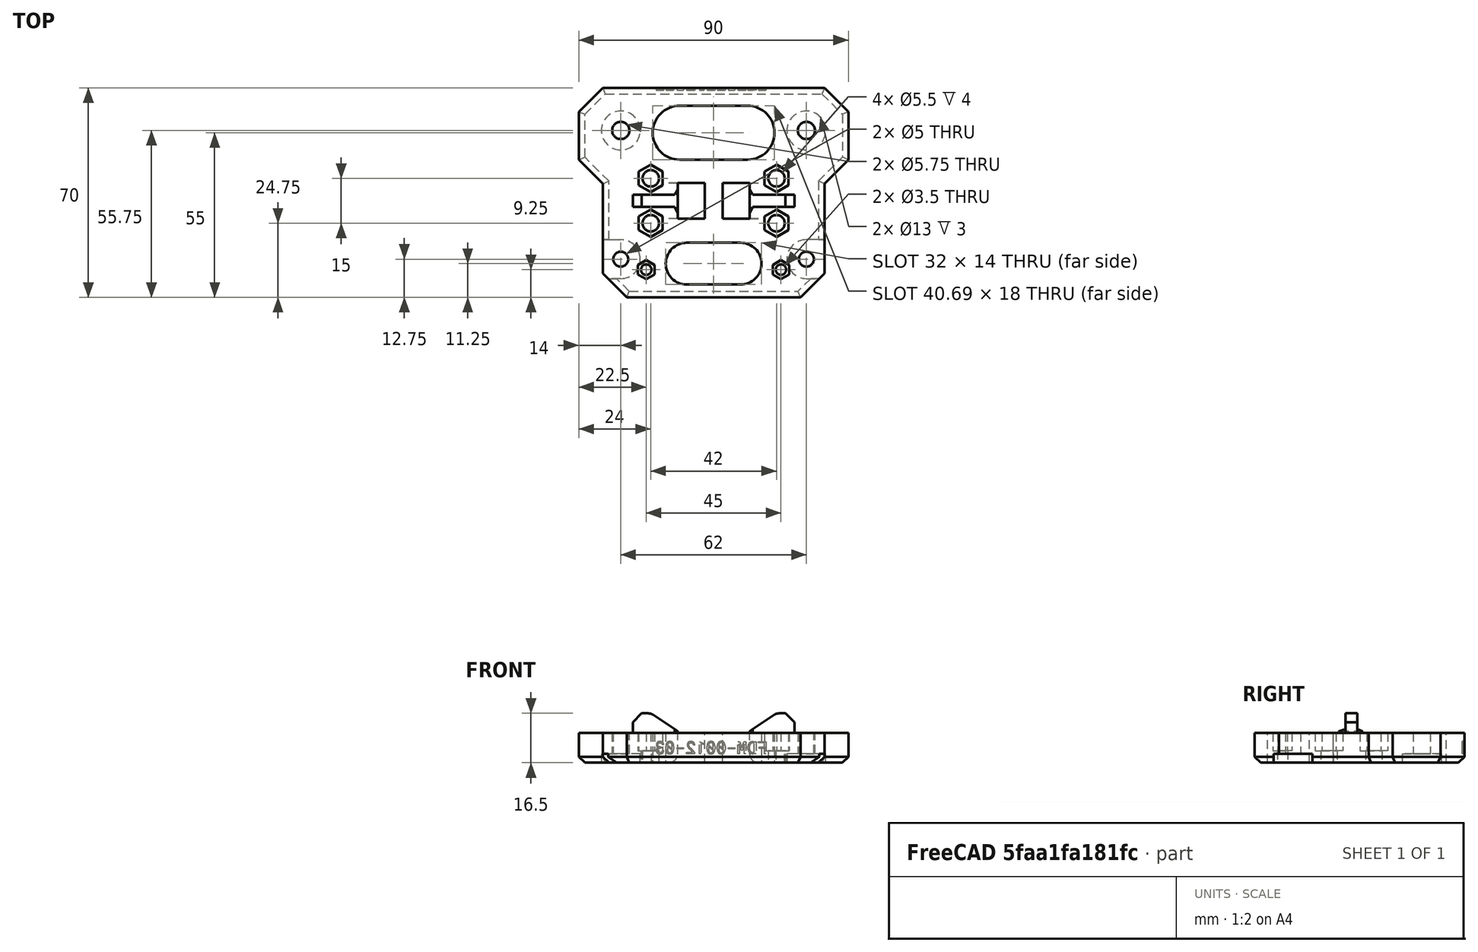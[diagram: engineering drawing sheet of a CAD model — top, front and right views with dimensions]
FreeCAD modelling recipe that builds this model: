
FCSTD DOCUMENT  (FreeCAD 0.20R29177 (Git))
Label: x-gantry-back
License: All rights reserved
LicenseURL: http://en.wikipedia.org/wiki/All_rights_reserved
objects: Sketcher::SketchObject×5, PartDesign::Plane×4, PartDesign::Chamfer×3, PartDesign::Pocket×3, PartDesign::Pad×2, Part::Part2DObjectPython×1, PartDesign::Fillet×1, PartDesign::Body×1, Mesh::Feature×1, Part::Extrusion×1, Part::Cut×1
note: 31 computed .brp shape members not serialized (recipe doc carries the construction recipe); baked Part::Feature solids carry a one-line shape summary decoded from their .brp

FEATURE [Sketcher::SketchObject] Sketch  label="Base"
  FullyConstrained = false
  MapMode = 5
  Support = -> [XY_Plane]
  sketch-geometry (58):
    g0: LineSegment StartX=0 StartY=0 StartZ=0 EndX=0 EndY=41.5 EndZ=0
    g1: LineSegment StartX=-31 StartY=41.5 StartZ=0 EndX=31 EndY=41.5 EndZ=0
    g2: Circle CenterX=-31 CenterY=41.5 CenterZ=0 NormalX=0 NormalY=0 NormalZ=1 AngleXU=0 Radius=2.875
    g3: Circle CenterX=31 CenterY=41.5 CenterZ=0 NormalX=0 NormalY=0 NormalZ=1 AngleXU=0 Radius=2.875
    g4: ArcOfCircle CenterX=-31 CenterY=4.5 CenterZ=0 NormalX=0 NormalY=0 NormalZ=1 AngleXU=0 Radius=2.5 StartAngle=2e-16 EndAngle=3.14159
    g5: ArcOfCircle CenterX=-31 CenterY=-1.5 CenterZ=0 NormalX=0 NormalY=0 NormalZ=1 AngleXU=0 Radius=2.5 StartAngle=3.14159 EndAngle=6.28319
    g6: LineSegment StartX=-33.5 StartY=4.5 StartZ=0 EndX=-33.5 EndY=-1.5 EndZ=0
    g7: LineSegment StartX=-28.5 StartY=4.5 StartZ=0 EndX=-28.5 EndY=-1.5 EndZ=0
    g8: Circle CenterX=-31 CenterY=41.5 CenterZ=0 NormalX=0 NormalY=0 NormalZ=1 AngleXU=0 Radius=12.5
    g9: Circle CenterX=31 CenterY=41.5 CenterZ=0 NormalX=0 NormalY=0 NormalZ=1 AngleXU=0 Radius=12.5
    g10: LineSegment StartX=45 StartY=55.75 StartZ=0 EndX=45 EndY=31.75 EndZ=0
    g11: LineSegment StartX=-45 StartY=31.75 StartZ=0 EndX=-45 EndY=55.75 EndZ=0
    g12: LineSegment StartX=-21 StartY=25.5 StartZ=0 EndX=-21 EndY=10.5 EndZ=0
    g13: LineSegment StartX=-12 StartY=24 StartZ=0 EndX=-3 EndY=24 EndZ=0
    g14: LineSegment StartX=-3 StartY=24 StartZ=0 EndX=-3 EndY=12 EndZ=0
    g15: LineSegment StartX=-3 StartY=12 StartZ=0 EndX=-12 EndY=12 EndZ=0
    g16: LineSegment StartX=-12 StartY=12 StartZ=0 EndX=-12 EndY=24 EndZ=0
    g17: Circle CenterX=-21 CenterY=25.5 CenterZ=0 NormalX=0 NormalY=0 NormalZ=1 AngleXU=0 Radius=2.75
    g18: Circle CenterX=-21 CenterY=10.5 CenterZ=0 NormalX=0 NormalY=0 NormalZ=1 AngleXU=0 Radius=2.75
    g19: LineSegment StartX=-21 StartY=18 StartZ=0 EndX=21 EndY=18 EndZ=0
    g20: LineSegment StartX=21 StartY=25.5 StartZ=0 EndX=21 EndY=10.5 EndZ=0
    g21: Circle CenterX=21 CenterY=25.5 CenterZ=0 NormalX=0 NormalY=0 NormalZ=1 AngleXU=0 Radius=2.75
    g22: Circle CenterX=21 CenterY=10.5 CenterZ=0 NormalX=0 NormalY=0 NormalZ=1 AngleXU=0 Radius=2.75
    g23: LineSegment StartX=3 StartY=24 StartZ=0 EndX=12 EndY=24 EndZ=0
    g24: LineSegment StartX=12 StartY=24 StartZ=0 EndX=12 EndY=12 EndZ=0
    g25: LineSegment StartX=12 StartY=12 StartZ=0 EndX=3 EndY=12 EndZ=0
    g26: LineSegment StartX=3 StartY=12 StartZ=0 EndX=3 EndY=24 EndZ=0
    g27: LineSegment StartX=-22.5 StartY=-5 StartZ=0 EndX=22.5 EndY=-5 EndZ=0
    g28: Circle CenterX=-22.5 CenterY=-5 CenterZ=0 NormalX=0 NormalY=0 NormalZ=1 AngleXU=0 Radius=1.75
    g29: Circle CenterX=22.5 CenterY=-5 CenterZ=0 NormalX=0 NormalY=0 NormalZ=1 AngleXU=0 Radius=1.75
    g30: LineSegment StartX=45 StartY=55.75 StartZ=0 EndX=45 EndY=31.75 EndZ=0
    g31: ArcOfCircle CenterX=31 CenterY=4.5 CenterZ=0 NormalX=0 NormalY=0 NormalZ=1 AngleXU=0 Radius=2.5 StartAngle=2e-16 EndAngle=3.14159
    g32: ArcOfCircle CenterX=31 CenterY=-1.5 CenterZ=0 NormalX=0 NormalY=0 NormalZ=1 AngleXU=0 Radius=2.5 StartAngle=3.14159 EndAngle=6.28319
    g33: LineSegment StartX=28.5 StartY=4.5 StartZ=0 EndX=28.5 EndY=-1.5 EndZ=0
    g34: LineSegment StartX=33.5 StartY=4.5 StartZ=0 EndX=33.5 EndY=-1.5 EndZ=0
    g35: LineSegment StartX=37 StartY=23.75 StartZ=0 EndX=37 EndY=-6.25 EndZ=0
    g36: LineSegment StartX=37 StartY=-6.25 StartZ=0 EndX=29 EndY=-14.25 EndZ=0
    g37: LineSegment StartX=-29 StartY=-14.25 StartZ=0 EndX=-37 EndY=-6.25 EndZ=0
    g38: LineSegment StartX=-37 StartY=-6.25 StartZ=0 EndX=-37 EndY=23.75 EndZ=0
    g39: LineSegment StartX=-37 StartY=23.75 StartZ=0 EndX=-45 EndY=31.75 EndZ=0
    g40: LineSegment StartX=37 StartY=23.75 StartZ=0 EndX=45 EndY=31.75 EndZ=0
    g41: LineSegment StartX=-29 StartY=-14.25 StartZ=0 EndX=29 EndY=-14.25 EndZ=0
    g42: ArcOfCircle CenterX=-9 CenterY=-3 CenterZ=0 NormalX=0 NormalY=0 NormalZ=1 AngleXU=0 Radius=7 StartAngle=1.5708 EndAngle=4.71239
    g43: ArcOfCircle CenterX=9 CenterY=-3 CenterZ=0 NormalX=0 NormalY=0 NormalZ=1 AngleXU=0 Radius=7 StartAngle=4.71239 EndAngle=7.85398
    g44: LineSegment StartX=-9 StartY=-10 StartZ=0 EndX=9 EndY=-10 EndZ=0
    g45: LineSegment StartX=-9 StartY=4 StartZ=0 EndX=9 EndY=4 EndZ=0
    g46: ArcOfCircle CenterX=-11.3452 CenterY=40.75 CenterZ=0 NormalX=0 NormalY=0 NormalZ=1 AngleXU=0 Radius=9 StartAngle=1.5708 EndAngle=4.71239
    g47: ArcOfCircle CenterX=11.3452 CenterY=40.75 CenterZ=0 NormalX=0 NormalY=0 NormalZ=1 AngleXU=0 Radius=9 StartAngle=4.71239 EndAngle=7.85398
    g48: LineSegment StartX=-11.3452 StartY=31.75 StartZ=0 EndX=11.3452 EndY=31.75 EndZ=0
    g49: LineSegment StartX=-11.3452 StartY=49.75 StartZ=0 EndX=11.3452 EndY=49.75 EndZ=0
    g50: LineSegment StartX=45 StartY=55.75 StartZ=0 EndX=-45 EndY=55.75 EndZ=0
    g51: Circle CenterX=-31 CenterY=-1.5 CenterZ=0 NormalX=0 NormalY=0 NormalZ=1 AngleXU=0 Radius=2.5
    g52: Circle CenterX=31 CenterY=-1.5 CenterZ=0 NormalX=0 NormalY=0 NormalZ=1 AngleXU=0 Radius=2.5
    g53: LineSegment StartX=-45 StartY=31.75 StartZ=0 EndX=-45 EndY=47.75 EndZ=0
    g54: LineSegment StartX=-45 StartY=47.75 StartZ=0 EndX=-37 EndY=55.75 EndZ=0
    g55: LineSegment StartX=-37 StartY=55.75 StartZ=0 EndX=37 EndY=55.75 EndZ=0
    g56: LineSegment StartX=37 StartY=55.75 StartZ=0 EndX=45 EndY=47.75 EndZ=0
    g57: LineSegment StartX=45 StartY=47.75 StartZ=0 EndX=45 EndY=31.75 EndZ=0
  constraints (149):
    c: Coincident(g0,g-1)
    c: PointOnObject(g0,g1)
    c: Symmetric(g1,g1,g0)
    c: DistanceY(g0,g0) = 41.5
    c: DistanceX(g1,g1) = 62
    c: Coincident(g2,g1)
    c: Coincident(g3,g1)
    c: Tangent(g4,g7)
    c: Tangent(g4,g6)
    c: Tangent(g6,g5)
    c: Tangent(g7,g5)
    c: Vertical(g6)
    c: Coincident(g8,g2)
    c: Coincident(g9,g3)
    c: Diameter(g4) = 5
    c: DistanceY(g5,g4) = 6
    c: Diameter(g3) = 5.75
    c: Diameter(g2) = 5.75
    c: Diameter(g9) = 25
    c: Diameter(g8) = 25
    c: Vertical(g10)
    c: Vertical(g11)
    c: Symmetric(g11,g10,g-2)
    c: Equal(g10,g11)
    c: DistanceX(g11,g10) = 90
    c: DistanceY(g3,g10) = 14.25
    c: DistanceY(g12,g12) = 15
    c: Coincident(g13,g14)
    c: Coincident(g14,g15)
    c: Coincident(g15,g16)
    c: Coincident(g16,g13)
    c: Horizontal(g13)
    c: Horizontal(g15)
    c: Vertical(g14)
    c: DistanceX(g13,g13) = 9
    c: DistanceY(g16,g16) = 12
    c: Coincident(g17,g12)
    c: Coincident(g18,g12)
    c: Diameter(g17) = 5.5
    c: Diameter(g18) = 5.5
    c: PointOnObject(g19,g12)
    c: Symmetric(g19,g19,g-2)
    c: Symmetric(g17,g18,g19)
    c: Symmetric(g13,g15,g19)
    c: PointOnObject(g19,g20)
    c: Symmetric(g20,g20,g19)
    c: DistanceY(g20,g20) = 15
    c: Coincident(g22,g20)
    c: Diameter(g21) = 5.5
    c: Diameter(g22) = 5.5
    c: Distance(g13,g0) = 3
    c: Distance(g17,g0) = 21
    c: Coincident(g23,g24)
    c: Coincident(g24,g25)
    c: Coincident(g25,g26)
    c: Coincident(g26,g23)
    c: Horizontal(g23)
    c: Horizontal(g25)
    c: Vertical(g24)
    c: DistanceX(g23,g23) = 9
    c: DistanceY(g26,g26) = 12
    c: DistanceX(g-1,g23) = 3
    c: Symmetric(g23,g25,g19)
    c: Symmetric(g27,g27,g-2)
    c: DistanceY(g27,g-1) = 5
    c: DistanceX(g27,g27) = 45
    c: Coincident(g28,g27)
    c: Coincident(g29,g27)
    c: Diameter(g29) = 3.5
    c: DistanceY(g0,g4) = 4.5
    c: Vertical(g5,g4)
    c: Vertical(g4,g2)
    c: Tangent(g31,g34)
    c: Tangent(g31,g33)
    c: Tangent(g33,g32)
    c: Tangent(g34,g32)
    c: Vertical(g33)
    c: Equal(g4,g31) = 5
    c: Vertical(g32,g31)
    c: Horizontal(g31,g4)
    c: Vertical(g31,g3)
    c: Horizontal(g32,g5)
    c: Vertical(g35)
    c: Coincident(g36,g35)
    c: Coincident(g38,g37)
    c: Vertical(g38)
    c: Coincident(g39,g38)
    c: Coincident(g40,g35)
    c: Horizontal(g40,g39)
    c: Horizontal(g35,g38)
    c: DistanceX(g38,g35) = 74
    c: DistanceY(g36,g30) = 70
    c: Coincident(g41,g37)
    c: Coincident(g41,g36)
    c: Horizontal(g41)
    c: Angle(g35,g36) = 2.35619
    c: Angle(g37,g38) = 2.35619
    c: Horizontal(g37,g35)
    c: Coincident(g39,g11)
    c: Coincident(g30,g40)
    c: Vertical(g30)
    c: Angle(g30,g40) = 2.35619
    c: Angle(g39,g11) = 2.35619
    c: DistanceY(g36,g35) = 8
    c: DistanceY(g35,g35) = 30
    c: Equal(g28,g29)
    c: Tangent(g42,g45) = 1.5708
    c: Tangent(g42,g44) = -1.5708
    c: Tangent(g44,g43) = -1.5708
    c: Tangent(g45,g43) = 1.5708
    c: Horizontal(g44)
    c: Symmetric(g42,g43,g0)
    c: Diameter(g43) = 14
    c: DistanceX(g45,g45) = 18
    c: DistanceY(g43,g0) = 3
    c: Vertical(g21,g22)
    c: Horizontal(g21,g17)
    c: Tangent(g46,g49) = 1.5708
    c: Tangent(g46,g48) = -1.5708
    c: Tangent(g48,g47) = -1.5708
    c: Tangent(g49,g47) = 1.5708
    c: Horizontal(g48)
    c: Symmetric(g46,g47,g-2)
    c: Radius(g47) = 9
    c: DistanceY(g47,g30) = 6
    c: Coincident(g50,g11)
    c: DistanceY(g0,g19) = 18  'BeltY'
    c: Coincident(g10,g30)
    c: Coincident(g10,g50)
    c: Horizontal(g1)
    c: Coincident(g51,g5)
    c: Equal(g51,g5)
    c: Coincident(g52,g32)
    c: Equal(g52,g32)
    c: Coincident(g39,g53)
    c: PointOnObject(g53,g11)
    c: Coincident(g53,g54)
    c: PointOnObject(g54,g50)
    c: Coincident(g54,g55)
    c: PointOnObject(g55,g50)
    c: Coincident(g55,g56)
    c: PointOnObject(g56,g10)
    c: Coincident(g56,g57)
    c: Coincident(g57,g40)
    c: Vertical(g54,g38)
    c: Vertical(g55,g35)
    c: Equal(g40,g56)
    c: Equal(g54,g39)
    c: DistanceY(g51,g2) = 43
FEATURE [PartDesign::Pad] Pad
  AllowMultiFace = false
  Direction = (0,0,1)
  Length = 10
  Length2 = 100
  Profile = -> Sketch
  Refine = true
  Type = 0
FEATURE [PartDesign::Plane] DatumPlane  label="DatumPlaneFront"
  Length = 107.076
  MapMode = 5
  Placement = pos=(0,0,10) rot=(0,0,1;0rad)
  ResizeMode = 0
  Support = -> [Pad]
  Width = 98.0763
FEATURE [Sketcher::SketchObject] Sketch002  label="M5Nuts"
  FullyConstrained = true
  MapMode = 5
  Placement = pos=(0,0,10) rot=(0,0,1;0rad)
  Support = -> [DatumPlane]
  expr: Constraints[124] = <<Base>>.Constraints.BeltY
  sketch-geometry (43):
    g0: LineSegment StartX=-17 StartY=23.1906 StartZ=0 EndX=-17 EndY=27.8094 EndZ=0
    g1: LineSegment StartX=-17 StartY=27.8094 StartZ=0 EndX=-21 EndY=30.1188 EndZ=0
    g2: LineSegment StartX=-21 StartY=30.1188 StartZ=0 EndX=-25 EndY=27.8094 EndZ=0
    g3: LineSegment StartX=-25 StartY=27.8094 StartZ=0 EndX=-25 EndY=23.1906 EndZ=0
    g4: LineSegment StartX=-25 StartY=23.1906 StartZ=0 EndX=-21 EndY=20.8812 EndZ=0
    g5: LineSegment StartX=-21 StartY=20.8812 StartZ=0 EndX=-17 EndY=23.1906 EndZ=0
    g6: Circle CenterX=-21 CenterY=25.5 CenterZ=0 NormalX=0 NormalY=0 NormalZ=1 AngleXU=0 Radius=4.6188
    g7: LineSegment StartX=-17 StartY=8.1906 StartZ=0 EndX=-17 EndY=12.8094 EndZ=0
    g8: LineSegment StartX=-17 StartY=12.8094 StartZ=0 EndX=-21 EndY=15.1188 EndZ=0
    g9: LineSegment StartX=-21 StartY=15.1188 StartZ=0 EndX=-25 EndY=12.8094 EndZ=0
    g10: LineSegment StartX=-25 StartY=12.8094 StartZ=0 EndX=-25 EndY=8.1906 EndZ=0
    g11: LineSegment StartX=-25 StartY=8.1906 StartZ=0 EndX=-21 EndY=5.8812 EndZ=0
    g12: LineSegment StartX=-21 StartY=5.8812 StartZ=0 EndX=-17 EndY=8.1906 EndZ=0
    g13: Circle CenterX=-21 CenterY=10.5 CenterZ=0 NormalX=0 NormalY=0 NormalZ=1 AngleXU=0 Radius=4.6188
    g14: LineSegment StartX=-19.75 StartY=-6.58771 StartZ=0 EndX=-19.75 EndY=-3.41229 EndZ=0
    g15: LineSegment StartX=-19.75 StartY=-3.41229 StartZ=0 EndX=-22.5 EndY=-1.82457 EndZ=0
    g16: LineSegment StartX=-22.5 StartY=-1.82457 StartZ=0 EndX=-25.25 EndY=-3.41229 EndZ=0
    g17: LineSegment StartX=-25.25 StartY=-3.41229 StartZ=0 EndX=-25.25 EndY=-6.58771 EndZ=0
    g18: LineSegment StartX=-25.25 StartY=-6.58771 StartZ=0 EndX=-22.5 EndY=-8.17543 EndZ=0
    g19: LineSegment StartX=-22.5 StartY=-8.17543 StartZ=0 EndX=-19.75 EndY=-6.58771 EndZ=0
    g20: Circle CenterX=-22.5 CenterY=-5 CenterZ=0 NormalX=0 NormalY=0 NormalZ=1 AngleXU=0 Radius=3.17543
    g21: LineSegment StartX=25.25 StartY=-6.58771 StartZ=0 EndX=25.25 EndY=-3.41229 EndZ=0
    g22: LineSegment StartX=25.25 StartY=-3.41229 StartZ=0 EndX=22.5 EndY=-1.82457 EndZ=0
    g23: LineSegment StartX=22.5 StartY=-1.82457 StartZ=0 EndX=19.75 EndY=-3.41229 EndZ=0
    g24: LineSegment StartX=19.75 StartY=-3.41229 StartZ=0 EndX=19.75 EndY=-6.58771 EndZ=0
    g25: LineSegment StartX=19.75 StartY=-6.58771 StartZ=0 EndX=22.5 EndY=-8.17543 EndZ=0
    g26: LineSegment StartX=22.5 StartY=-8.17543 StartZ=0 EndX=25.25 EndY=-6.58771 EndZ=0
    g27: Circle CenterX=22.5 CenterY=-5 CenterZ=0 NormalX=0 NormalY=0 NormalZ=1 AngleXU=0 Radius=3.17543
    g28: LineSegment StartX=25 StartY=8.1906 StartZ=0 EndX=25 EndY=12.8094 EndZ=0
    g29: LineSegment StartX=25 StartY=12.8094 StartZ=0 EndX=21 EndY=15.1188 EndZ=0
    g30: LineSegment StartX=21 StartY=15.1188 StartZ=0 EndX=17 EndY=12.8094 EndZ=0
    g31: LineSegment StartX=17 StartY=12.8094 StartZ=0 EndX=17 EndY=8.1906 EndZ=0
    g32: LineSegment StartX=17 StartY=8.1906 StartZ=0 EndX=21 EndY=5.8812 EndZ=0
    g33: LineSegment StartX=21 StartY=5.8812 StartZ=0 EndX=25 EndY=8.1906 EndZ=0
    g34: Circle CenterX=21 CenterY=10.5 CenterZ=0 NormalX=0 NormalY=0 NormalZ=1 AngleXU=0 Radius=4.6188
    g35: LineSegment StartX=25 StartY=23.1906 StartZ=0 EndX=25 EndY=27.8094 EndZ=0
    g36: LineSegment StartX=25 StartY=27.8094 StartZ=0 EndX=21 EndY=30.1188 EndZ=0
    g37: LineSegment StartX=21 StartY=30.1188 StartZ=0 EndX=17 EndY=27.8094 EndZ=0
    g38: LineSegment StartX=17 StartY=27.8094 StartZ=0 EndX=17 EndY=23.1906 EndZ=0
    g39: LineSegment StartX=17 StartY=23.1906 StartZ=0 EndX=21 EndY=20.8812 EndZ=0
    g40: LineSegment StartX=21 StartY=20.8812 StartZ=0 EndX=25 EndY=23.1906 EndZ=0
    g41: Circle CenterX=21 CenterY=25.5 CenterZ=0 NormalX=0 NormalY=0 NormalZ=1 AngleXU=0 Radius=4.6188
    g42: LineSegment StartX=-21 StartY=18 StartZ=0 EndX=21 EndY=18 EndZ=0
  constraints (102):
    c: Coincident(g0,g1)
    c: Coincident(g1,g2)
    c: Coincident(g2,g3)
    c: Coincident(g3,g4)
    c: Coincident(g4,g5)
    c: Coincident(g5,g0)
    c: Equal(g0, g1-g5) x5
    c: PointOnObject(g0,g6)
    c: PointOnObject(g1,g6)
    c: PointOnObject(g2,g6)
    c: PointOnObject(g3,g6)
    c: PointOnObject(g4,g6)
    c: PointOnObject(g5,g6)
    c: Coincident(g7,g8)
    c: Coincident(g8,g9)
    c: Coincident(g9,g10)
    c: Coincident(g10,g11)
    c: Coincident(g11,g12)
    c: Coincident(g12,g7)
    c: Equal(g7, g8-g12) x5
    c: PointOnObject(g7,g13)
    c: PointOnObject(g8,g13)
    c: PointOnObject(g9,g13)
    c: PointOnObject(g10,g13)
    c: PointOnObject(g11,g13)
    c: PointOnObject(g12,g13)
    c: Coincident(g14,g15)
    c: Coincident(g15,g16)
    c: Coincident(g16,g17)
    c: Coincident(g17,g18)
    c: Coincident(g18,g19)
    c: Coincident(g19,g14)
    c: Equal(g14, g15-g19) x5
    c: PointOnObject(g14,g20)
    c: PointOnObject(g15,g20)
    c: PointOnObject(g16,g20)
    c: PointOnObject(g17,g20)
    c: PointOnObject(g18,g20)
    c: PointOnObject(g19,g20)
    c: Coincident(g21,g22)
    c: Coincident(g22,g23)
    c: Coincident(g23,g24)
    c: Coincident(g24,g25)
    c: Coincident(g25,g26)
    c: Coincident(g26,g21)
    c: Equal(g21, g22-g26) x5
    c: PointOnObject(g21,g27)
    c: PointOnObject(g22,g27)
    c: PointOnObject(g23,g27)
    c: PointOnObject(g24,g27)
    c: PointOnObject(g25,g27)
    c: PointOnObject(g26,g27)
    c: Coincident(g28,g29)
    c: Coincident(g29,g30)
    c: Coincident(g30,g31)
    c: Coincident(g31,g32)
    c: Coincident(g32,g33)
    c: Coincident(g33,g28)
    c: Equal(g28, g29-g33) x5
    c: PointOnObject(g28,g34)
    c: PointOnObject(g29,g34)
    c: PointOnObject(g30,g34)
    c: PointOnObject(g31,g34)
    c: PointOnObject(g32,g34)
    c: PointOnObject(g33,g34)
    c: Coincident(g35,g36)
    c: Coincident(g36,g37)
    c: Coincident(g37,g38)
    c: Coincident(g38,g39)
    c: Coincident(g39,g40)
    c: Coincident(g40,g35)
    c: Equal(g35, g36-g40) x5
    c: PointOnObject(g35,g41)
    c: PointOnObject(g36,g41)
    c: PointOnObject(g37,g41)
    c: PointOnObject(g38,g41)
    c: PointOnObject(g39,g41)
    c: PointOnObject(g40,g41)
    c: Vertical(g10)
    c: Vertical(g3)
    c: Vertical(g17)
    c: Vertical(g24)
    c: Vertical(g31)
    c: Vertical(g38)
    c: DistanceX(g20,g-1) = 22.5
    c: DistanceX(g-1,g27) = 22.5
    c: DistanceX(g13,g-1) = 21
    c: DistanceY(g20,g-1) = 5
    c: DistanceY(g27,g-1) = 5
    c: DistanceX(g2,g0) = 8
    c: Equal(g6,g13)
    c: Equal(g13,g34)
    c: Equal(g34,g41)
    c: DistanceX(g17,g14) = 5.5
    c: Equal(g20,g27)
    c: Symmetric(g34,g13,g-2)
    c: Symmetric(g41,g6,g-2)
    c: DistanceY(g13,g6) = 15
    c: Symmetric(g42,g42,g-2)
    c: Vertical(g42,g6)
    c: DistanceY(g-1,g42) = 18
    c: Symmetric(g13,g6,g42)
FEATURE [Sketcher::SketchObject] Sketch007  label="M5SlotCutOuts"
  FullyConstrained = true
  MapMode = 5
  Support = -> [XY_Plane]
  sketch-geometry (15):
    g0: Circle CenterX=-31 CenterY=41.5 CenterZ=0 NormalX=0 NormalY=0 NormalZ=1 AngleXU=0 Radius=6.5
    g1: Circle CenterX=31 CenterY=41.5 CenterZ=0 NormalX=0 NormalY=0 NormalZ=1 AngleXU=0 Radius=6.5
    g2: LineSegment StartX=-31 StartY=41.5 StartZ=0 EndX=31 EndY=41.5 EndZ=0
    g3: ArcOfCircle CenterX=-31 CenterY=-1.5 CenterZ=0 NormalX=0 NormalY=0 NormalZ=1 AngleXU=0 Radius=6.5 StartAngle=3.14159 EndAngle=6.28319
    g4: ArcOfCircle CenterX=-31 CenterY=5.5 CenterZ=0 NormalX=0 NormalY=0 NormalZ=1 AngleXU=0 Radius=6.5 StartAngle=1e-16 EndAngle=3.14159
    g5: LineSegment StartX=-24.5 StartY=-1.5 StartZ=0 EndX=-24.5 EndY=5.5 EndZ=0
    g6: LineSegment StartX=-37.5 StartY=5.5 StartZ=0 EndX=-37.5 EndY=-1.5 EndZ=0
    g7: GeomPoint X=-31 Y=12 Z=0
    g8: GeomPoint X=-31 Y=-8 Z=0
    g9: ArcOfCircle CenterX=31 CenterY=5.5 CenterZ=0 NormalX=0 NormalY=0 NormalZ=1 AngleXU=0 Radius=6.5 StartAngle=0 EndAngle=3.14159
    g10: ArcOfCircle CenterX=31 CenterY=-1.5 CenterZ=0 NormalX=0 NormalY=0 NormalZ=1 AngleXU=0 Radius=6.5 StartAngle=3.14159 EndAngle=6.28319
    g11: LineSegment StartX=24.5 StartY=5.5 StartZ=0 EndX=24.5 EndY=-1.5 EndZ=0
    g12: LineSegment StartX=37.5 StartY=-1.5 StartZ=0 EndX=37.5 EndY=5.5 EndZ=0
    g13: Circle CenterX=-31 CenterY=-1.5 CenterZ=0 NormalX=0 NormalY=0 NormalZ=1 AngleXU=0 Radius=6.5
    g14: Circle CenterX=31 CenterY=-1.5 CenterZ=0 NormalX=0 NormalY=0 NormalZ=1 AngleXU=0 Radius=6.5
  constraints (33):
    c: Coincident(g2,g0)
    c: Coincident(g2,g1)
    c: Symmetric(g0,g1,g-2)
    c: DistanceX(g2,g2) = 62
    c: DistanceY(g-1,g0) = 41.5
    c: Diameter(g0) = 13
    c: Equal(g0,g1)
    c: Tangent(g3,g5) = -1.5708
    c: Tangent(g5,g4) = -1.5708
    c: Tangent(g4,g6) = -1.5708
    c: Tangent(g6,g3) = -1.5708
    c: Equal(g3,g4)
    c: Vertical(g5)
    c: PointOnObject(g7,g4)
    c: PointOnObject(g8,g3)
    c: Vertical(g8,g7)
    c: Vertical(g7,g4)
    c: Equal(g4,g0)
    c: DistanceY(g-1,g4) = 5.5
    c: DistanceY(g3,g4) = 7
    c: Vertical(g4,g0)
    c: Tangent(g9,g11) = -1.5708
    c: Tangent(g11,g10) = -1.5708
    c: Tangent(g10,g12) = -1.5708
    c: Tangent(g12,g9) = -1.5708
    c: Equal(g9,g10)
    c: Symmetric(g10,g3,g-2)
    c: Symmetric(g9,g4,g-2)
    c: Equal(g9,g4)
    c: Coincident(g13,g3)
    c: Equal(g13,g3)
    c: Coincident(g14,g10)
    c: Equal(g14,g10)
FEATURE [PartDesign::Plane] DatumPlane004  label="PartNumberPlane"
  Length = 93.7279
  MapMode = 5
  Placement = pos=(0,0,0) rot=(0.57735,0.57735,0.57735;2.0944rad)
  ResizeMode = 0
  Support = -> [YZ_Plane]
  Width = 62.7279
FEATURE [PartDesign::Plane] DatumPlane005  label="PrintPlane"
  Length = 107.076
  MapMode = 5
  Placement = pos=(0,0,0) rot=(1,0,0;3.14159rad)
  ResizeMode = 0
  Support = -> [Pad]
  Width = 98.0763
FEATURE [Part::Part2DObjectPython] ShapeString001  label="PN"  # Draft 2D object (typed FeaturePython)
  AttachmentOffset = pos=(56,3,18) rot=(0,1,0;1.5708rad)
  FontFile = ../../lib/fonts/RobotoMono-VariableFont_weight.ttf
  MapMode = 5
  Placement = pos=(18,56,3) rot=(0,0.707107,0.707107;3.14159rad)
  Size = 5
  String = FDM-0012-03
  Support = -> [YZ_Plane]
  Tracking = 0
FEATURE [PartDesign::Plane] DatumPlane007  label="DatumPlaneBack"
  Length = 107.076
  MapMode = 5
  Placement = pos=(0,0,0) rot=(1,0,0;3.14159rad)
  ResizeMode = 0
  Support = -> [Pad]
  Width = 98.0763
FEATURE [Sketcher::SketchObject] Sketch012
  FullyConstrained = true
  MapMode = 5
  Placement = pos=(0,0,10) rot=(0,0,1;0rad)
  Support = -> [DatumPlane]
  expr: Constraints[36] = <<Base>>.Constraints.BeltY
  sketch-geometry (13):
    g0: LineSegment StartX=-12 StartY=21.7872 StartZ=0 EndX=-13.0318 EndY=20 EndZ=0
    g1: LineSegment StartX=-13.0318 StartY=20 StartZ=0 EndX=-27 EndY=20 EndZ=0
    g2: LineSegment StartX=-27 StartY=20 StartZ=0 EndX=-27 EndY=16 EndZ=0
    g3: LineSegment StartX=-27 StartY=16 StartZ=0 EndX=-13.0318 EndY=16 EndZ=0
    g4: LineSegment StartX=-13.0318 StartY=16 StartZ=0 EndX=-12 EndY=13.7872 EndZ=0
    g5: LineSegment StartX=-12 StartY=13.7872 StartZ=0 EndX=-12 EndY=21.7872 EndZ=0
    g6: LineSegment StartX=12 StartY=21.7872 StartZ=0 EndX=12 EndY=13.7872 EndZ=0
    g7: LineSegment StartX=12 StartY=13.7872 StartZ=0 EndX=13.0318 EndY=16 EndZ=0
    g8: LineSegment StartX=13.0318 StartY=16 StartZ=0 EndX=27 EndY=16 EndZ=0
    g9: LineSegment StartX=27 StartY=16 StartZ=0 EndX=27 EndY=20 EndZ=0
    g10: LineSegment StartX=27 StartY=20 StartZ=0 EndX=13.0318 EndY=20 EndZ=0
    g11: LineSegment StartX=13.0318 StartY=20 StartZ=0 EndX=12 EndY=21.7872 EndZ=0
    g12: LineSegment StartX=-27 StartY=18 StartZ=0 EndX=27 EndY=18 EndZ=0
  constraints (38):
    c: Coincident(g0,g1)
    c: Horizontal(g1)
    c: Coincident(g1,g2)
    c: Vertical(g2)
    c: Coincident(g2,g3)
    c: Horizontal(g3)
    c: Coincident(g3,g4)
    c: Coincident(g4,g5)
    c: Coincident(g5,g0)
    c: Vertical(g5)
    c: DistanceX(g4,g-1) = 12
    c: DistanceY(g5,g5) = 8
    c: DistanceY(g2,g2) = 4
    c: Equal(g1,g3)
    c: Angle(g0,g5) = 0.523599
    c: Angle(g5,g4) = 0.436332
    c: DistanceX(g2,g4) = 15
    c: Vertical(g6)
    c: Coincident(g6,g7)
    c: Coincident(g7,g8)
    c: Horizontal(g8)
    c: Coincident(g8,g9)
    c: Coincident(g9,g10)
    c: Horizontal(g10)
    c: Coincident(g10,g11)
    c: Coincident(g11,g6)
    c: Equal(g10,g8)
    c: DistanceY(g6,g6) = 8
    c: DistanceY(g9,g9) = 4
    c: Angle(g6,g11) = 0.523599
    c: Angle(g7,g6) = 0.436332
    c: DistanceX(g-1,g6) = 12
    c: DistanceX(g6,g8) = 15
    c: PointOnObject(g12,g2)
    c: PointOnObject(g12,g9)
    c: Symmetric(g2,g1,g12)
    c: DistanceY(g-1,g12) = 18
    c: Symmetric(g8,g9,g12)
FEATURE [PartDesign::Pad] Pad003  label="PadBeltStandoff"
  BaseFeature = -> Pad
  Direction = (0,0,1)
  Length = 6.5
  Length2 = 100
  Profile = -> Sketch012
  Type = 0
FEATURE [PartDesign::Chamfer] Chamfer003  label="ChamferBeltStandoffSlope"
  Angle = 45
  Base = -> Pad003 [Edge152,Edge151]
  BaseFeature = -> Pad003
  ChamferType = 1
  FlipDirection = false
  Size = 6
  Size2 = 9
  SupportTransform = false
  UseAllEdges = false
FEATURE [PartDesign::Fillet] Fillet001  label="FilletBeltGuide"
  Base = -> Chamfer003 [Edge11,Edge158,Edge103,Edge119]
  BaseFeature = -> Chamfer003
  Radius = 3
  SupportTransform = false
  UseAllEdges = false
FEATURE [PartDesign::Chamfer] Chamfer004  label="ChamferBeltStandoffOuterSlope"
  Angle = 45
  Base = -> Fillet001 [Edge17,Edge136]
  BaseFeature = -> Fillet001
  ChamferType = 0
  FlipDirection = false
  Size = 3
  Size2 = 1
  SupportTransform = false
  UseAllEdges = false
FEATURE [PartDesign::Chamfer] Chamfer  label="ChamferOuterEdge"
  Angle = 30
  Base = -> Chamfer004 [Edge87,Edge83,Edge91,Edge95,Edge96,Edge93,Edge89,Edge85,Edge81,Edge77,Edge79,Edge75]
  BaseFeature = -> Chamfer004
  ChamferType = 0
  FlipDirection = false
  Size = 2
  Size2 = 1
  SupportTransform = false
  UseAllEdges = false
FEATURE [PartDesign::Pocket] Pocket006  label="PocketPartNumber"
  BaseFeature = -> Chamfer
  Direction = (-3e-16,-1,0)
  Length = 1
  Length2 = 100
  Profile = -> ShapeString001
  Type = 0
FEATURE [PartDesign::Pocket] Pocket  label="PocketM5Nuts"
  AllowMultiFace = false
  BaseFeature = -> Pocket006
  Direction = (0,0,-1)
  Length = 6
  Length2 = 100
  Profile = -> Sketch002
  ReferenceAxis = -> Sketch002 [N_Axis]
  Refine = true
  Type = 0
FEATURE [PartDesign::Pocket] Pocket004  label="PocketM5BoltHeads"
  AllowMultiFace = false
  BaseFeature = -> Pocket
  Direction = (0,0,-1)
  Length = 3
  Length2 = 100
  Profile = -> Sketch007
  Reversed = true
  Type = 0
FEATURE [PartDesign::Body] Body
  Group = -> [Sketch,Pad,DatumPlane005,DatumPlane,DatumPlane007,Sketch002,Sketch007,DatumPlane004,ShapeString001,Sketch012,Pad003,Chamfer003,Fillet001,Chamfer004,Chamfer,Pocket006,Pocket,Pocket004]
  Origin = -> Origin
  Tip = -> Pocket004
FEATURE [Mesh::Feature] Mesh  label="Body (Meshed)"
FEATURE [Sketcher::SketchObject] Sketch013
  ExternalGeometry = -> [Pocket004]
  FullyConstrained = true
  MapMode = 5
  Placement = pos=(0,0,3) rot=(1,0,0;3.14159rad)
  Support = -> [Pocket004]
  sketch-geometry (10):
    g0: Circle CenterX=-31 CenterY=1.5 CenterZ=0 NormalX=0 NormalY=0 NormalZ=1 AngleXU=0 Radius=6.5
    g1: Circle CenterX=31 CenterY=1.5 CenterZ=0 NormalX=0 NormalY=0 NormalZ=1 AngleXU=0 Radius=6.5
    g2: LineSegment StartX=31 StartY=8 StartZ=0 EndX=31 EndY=-5 EndZ=0
    g3: LineSegment StartX=31 StartY=8 StartZ=0 EndX=54 EndY=8 EndZ=0
    g4: LineSegment StartX=54 StartY=8 StartZ=0 EndX=54 EndY=-5 EndZ=0
    g5: LineSegment StartX=54 StartY=-5 StartZ=0 EndX=31 EndY=-5 EndZ=0
    g6: LineSegment StartX=-31 StartY=-5 StartZ=0 EndX=-31 EndY=8 EndZ=0
    g7: LineSegment StartX=-31 StartY=8 StartZ=0 EndX=-54 EndY=8 EndZ=0
    g8: LineSegment StartX=-54 StartY=8 StartZ=0 EndX=-54 EndY=-5 EndZ=0
    g9: LineSegment StartX=-54 StartY=-5 StartZ=0 EndX=-31 EndY=-5 EndZ=0
  constraints (28):
    c: Coincident(g0,g-4)
    c: PointOnObject(g-4,g0)
    c: Coincident(g1,g-3)
    c: PointOnObject(g-3,g1)
    c: Vertical(g2)
    c: PointOnObject(g2,g1)
    c: PointOnObject(g2,g1)
    c: PointOnObject(g1,g2)
    c: Coincident(g3,g2)
    c: Horizontal(g3)
    c: Coincident(g4,g3)
    c: Vertical(g4)
    c: Coincident(g5,g4)
    c: Coincident(g5,g2)
    c: Horizontal(g5)
    c: Distance(g3) = 23
    c: PointOnObject(g6,g0)
    c: PointOnObject(g6,g0)
    c: Vertical(g6)
    c: PointOnObject(g0,g6)
    c: Coincident(g6,g7)
    c: Horizontal(g7)
    c: Coincident(g7,g8)
    c: Vertical(g8)
    c: Coincident(g8,g9)
    c: Coincident(g9,g6)
    c: Horizontal(g9)
    c: Distance(g7) = 23
FEATURE [Part::Extrusion] Extrude
  Base = -> Sketch013
  Dir = (0,0,-1)
  DirMode = 2
  FaceMakerClass = Part::FaceMakerBullseye
  LengthFwd = 3
  LengthRev = 0
  Solid = true
  Symmetric = false
FEATURE [Part::Cut] Cut
  Base = -> Body
  Refine = true
  Tool = -> Extrude
